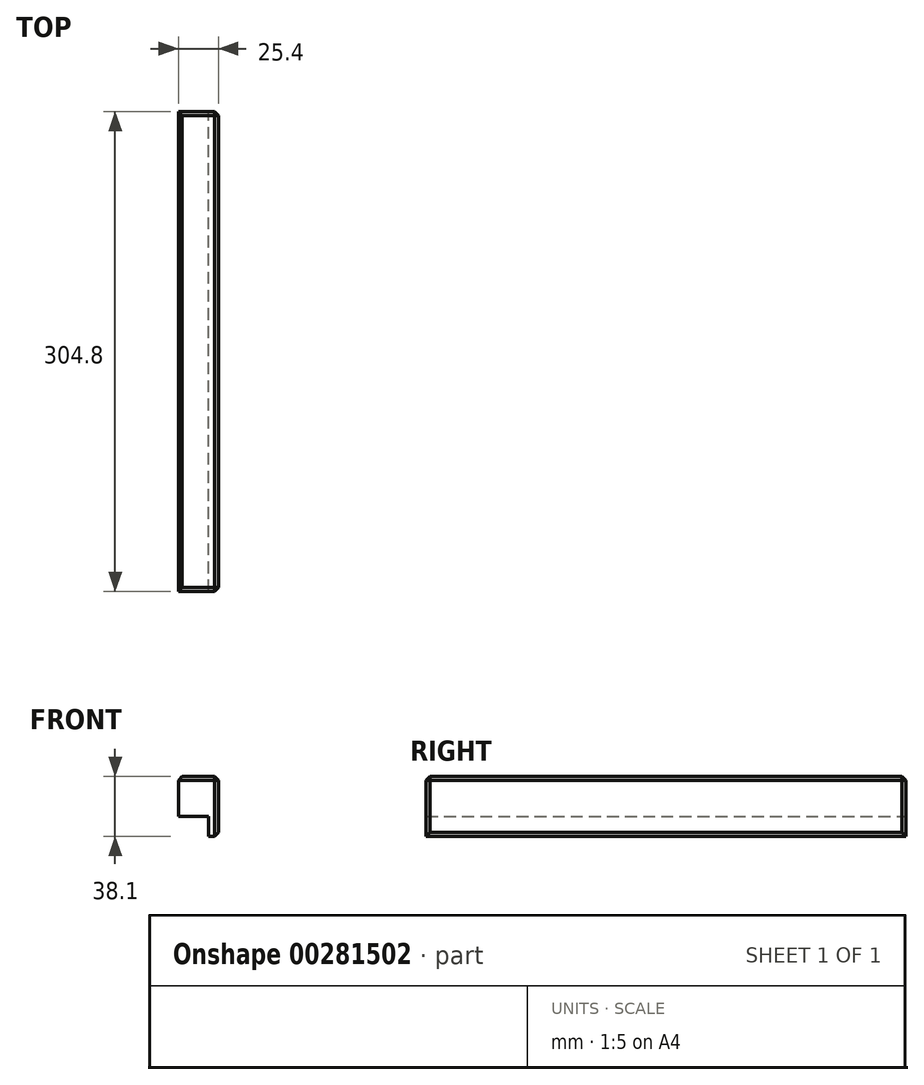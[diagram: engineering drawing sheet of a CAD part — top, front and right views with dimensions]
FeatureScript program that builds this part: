
annotation { "Feature Type Name" : "Feature", "Feature Type Description" : "" }
export const myFeature = defineFeature(function(context is Context, id is Id, definition is map)
    precondition{}
    {
        {
            var Q0;
            Q0=qCreatedBy(makeId("Front.planeOp"),FACE);
            var sketch = newSketch(context, id + "F0", { "sketchPlane" : qUnion([Q0])});
            skLineSegment(sketch, "E0", {"start": v(-25.4, 19.05) * mm, "end": v(0, 19.05) * mm});
            skLineSegment(sketch, "E1", {"start": v(0, 19.05) * mm, "end": v(0, -19.05) * mm});
            skLineSegment(sketch, "E2", {"start": v(0, -19.05) * mm, "end": v(-6.35, -19.05) * mm});
            skLineSegment(sketch, "E3", {"start": v(-6.35, -19.05) * mm, "end": v(-6.35, -6.35) * mm});
            skLineSegment(sketch, "E4", {"start": v(-6.35, -6.35) * mm, "end": v(-25.4, -6.35) * mm});
            skLineSegment(sketch, "E5", {"start": v(-25.4, -6.35) * mm, "end": v(-25.4, 19.05) * mm});
            skSolve(sketch);
        }
        {
            var Q0;
            Q0 = qSketchRegion(id + "F0", true);
            extrude(context, id + "F1", {"entities" : qUnion([Q0]), "endBound" : BoundingType.SYMMETRIC, "depth" : 304.8 * mm});
        }
        {
            var Q0;
            Q0=makeQuery(id+"F1.opExtrude","SWEPT_FACE",FACE,{"disambiguationData":[OSD([sQuery(id+"F0.wireOp",EDGE,"E1")])]});
            var Q1;
            Q1=makeQuery(id+"F1.opExtrude","SWEPT_FACE",FACE,{"disambiguationData":[OSD([sQuery(id+"F0.wireOp",EDGE,"E0")])]});
            chamfer(context, id + "F2", {"entities" : qUnion([Q0, Q1]), "width" : 2.54 * mm, "tangentPropagation" : true});
        }
    });
